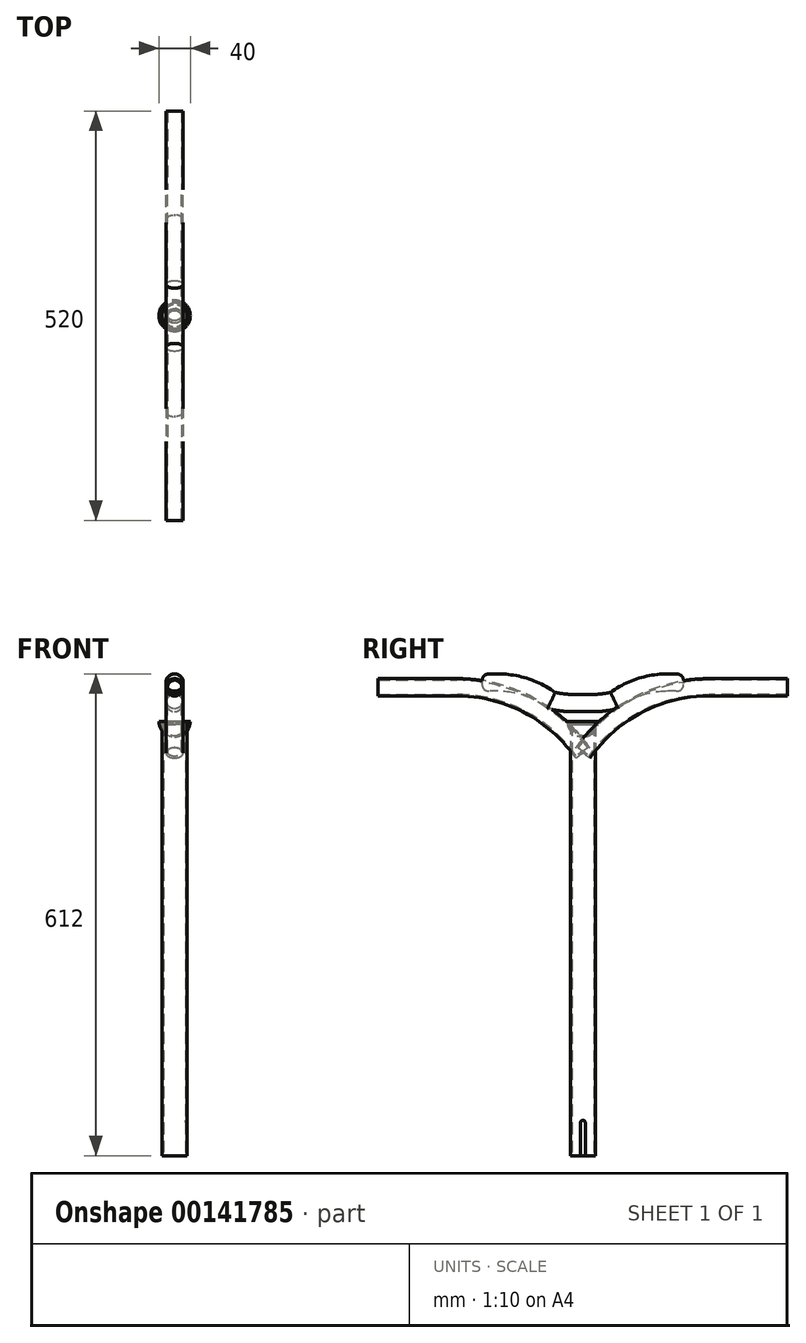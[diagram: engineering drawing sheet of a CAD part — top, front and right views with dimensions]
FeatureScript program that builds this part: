
annotation { "Feature Type Name" : "Feature", "Feature Type Description" : "" }
export const myFeature = defineFeature(function(context is Context, id is Id, definition is map)
    precondition{}
    {
        {
            var Q0;
            Q0=qCreatedBy(makeId("Top.planeOp"),FACE);
            var sketch = newSketch(context, id + "F0", { "sketchPlane" : qUnion([Q0])});
            skCircle(sketch, "E0", {"center": v(0, 0) * mm, "radius": 16 * mm});
            skSolve(sketch);
        }
        {
            var Q0;
            Q0 = qSketchRegion(id + "F0", true);
            extrude(context, id + "F1", {"entities" : qUnion([Q0]), "depth" : 550 * mm});
        }
        {
            var Q0;
            Q0=makeQuery(id+"F1.opExtrude","CAP_FACE",FACE,{"disambiguationData":[OSD([sQuery(id+"F0.wireOp",EDGE,"E0")])],"isStart":true});
            shell(context, id + "F2", {"entities" : qUnion([Q0]), "thickness" : 2 * mm});
        }
        {
            var Q0;
            Q0=qCreatedBy(makeId("Right.planeOp"),FACE);
            var sketch = newSketch(context, id + "F3", { "sketchPlane" : qUnion([Q0])});
            skLineSegment(sketch, "E1.bottom", {"start": v(-3, 0) * mm, "end": v(3, 0) * mm});
            skLineSegment(sketch, "E1.top", {"start": v(0, 45) * mm, "end": v(0, 45) * mm});
            skLineSegment(sketch, "E1.left", {"start": v(-3, 0) * mm, "end": v(-3, 42) * mm});
            skLineSegment(sketch, "E1.right", {"start": v(3, 0) * mm, "end": v(3, 42) * mm});
            skPoint(sketch, "E2.visualSharp", {"position": v(-3, 45) * mm});
            skArc(sketch, "E2.filletArc", {"start": v(0, 45) * mm, "mid": v(-2.12, 44.12) * mm, "end": v(-3, 42) * mm});
            skPoint(sketch, "E3.visualSharp", {"position": v(3, 45) * mm});
            skArc(sketch, "E3.filletArc", {"start": v(3, 42) * mm, "mid": v(2.12, 44.12) * mm, "end": v(0, 45) * mm});
            skSolve(sketch);
        }
        {
            var Q0;
            Q0 = qSketchRegion(id + "F3", true);
            extrude(context, id + "F4", {"entities" : qUnion([Q0]), "operationType" : NewBodyOperationType.REMOVE, "endBound" : BoundingType.THROUGH_ALL, "depth" : 25 * mm});
        }
        {
            var Q0;
            Q0=qCreatedBy(makeId("Right.planeOp"),FACE);
            var sketch = newSketch(context, id + "F5", { "sketchPlane" : qUnion([Q0])});
            skArc(sketch, "E4", {"start": v(160, 595) * mm, "mid": v(69.75, 572.86) * mm, "end": v(0, 511.47) * mm});
            skLineSegment(sketch, "E5", {"start": v(160, 595) * mm, "end": v(260, 595) * mm});
            skSolve(sketch);
        }
        {
            var Q0;
            Q0=sQuery(id+"F5.wireOp",VERTEX,"E5.end");
            var Q1;
            Q1=qCreatedBy(makeId("Front.planeOp"),FACE);
            cPlane(context, id + "F6", {"entities" : qUnion([Q0, Q1]), "cplaneType" : CPlaneType.PLANE_POINT, "offset" : 25 * mm, "width" : 150 * mm, "height" : 150 * mm});
        }
        {
            var Q0;
            Q0=qCreatedBy(id+"F6.planeOp",FACE);
            var sketch = newSketch(context, id + "F7", { "sketchPlane" : qUnion([Q0])});
            skCircle(sketch, "E6", {"center": v(0, 595) * mm, "radius": 11 * mm});
            skSolve(sketch);
        }
        {
            var Q0;
            Q0 = qSketchRegion(id + "F7", true);
            var Q1;
            Q1 = qConstructionFilter(qBodyType(qCreatedBy(id + "F5" ,EDGE), BodyType.WIRE), ConstructionObject.NO);
            sweep(context, id + "F8", {"profiles" : qUnion([Q0]), "path" : qUnion([Q1])});
        }
        {
            var Q0;
            Q0=makeQuery(id+"F8.opSweep","CAP_FACE",FACE,{"disambiguationData":[OSD([sQuery(id+"F5.wireOp",VERTEX,"E5.end"),sQuery(id+"F7.wireOp",EDGE,"E6")])],"isStart":true});
            shell(context, id + "F9", {"entities" : qUnion([Q0]), "thickness" : 2 * mm});
        }
        {
            var Q0;
            Q0=makeQuery(id+"F8.opSweep","SWEPT_BODY",BODY,{"disambiguationData":[OSD([sQuery(id+"F5.wireOp",EDGE,"E5"),sQuery(id+"F7.wireOp",EDGE,"E6")])]});
            var Q1;
            Q1=qCreatedBy(makeId("Front.planeOp"),FACE);
            mirror(context, id + "F10", {"entities" : qUnion([Q0]), "mirrorPlane" : qUnion([Q1])});
        }
        {
            var Q0;
            Q0=qCreatedBy(makeId("Right.planeOp"),FACE);
            var sketch = newSketch(context, id + "F11", { "sketchPlane" : qUnion([Q0])});
            skLineSegment(sketch, "E7", {"start": v(-128, 601) * mm, "end": v(-108, 601) * mm});
            skArc(sketch, "E8", {"start": v(-39.86, 578.4) * mm, "mid": v(-72.1, 595.2) * mm, "end": v(-108, 601) * mm});
            skArc(sketch, "E9", {"start": v(-39.86, 578.4) * mm, "mid": v(-26.28, 575.85) * mm, "end": v(-12.5, 575) * mm});
            skLineSegment(sketch, "E10", {"start": v(-12.5, 575) * mm, "end": v(0, 575) * mm});
            skLineSegment(sketch, "E11.MirrorCS", {"start": v(12.5, 575) * mm, "end": v(0, 575) * mm});
            skArc(sketch, "E12.MirrorCS", {"start": v(39.86, 578.4) * mm, "mid": v(26.28, 575.85) * mm, "end": v(12.5, 575) * mm});
            skArc(sketch, "E13.MirrorCS", {"start": v(39.86, 578.4) * mm, "mid": v(72.1, 595.2) * mm, "end": v(108, 601) * mm});
            skLineSegment(sketch, "E14.MirrorCS", {"start": v(128, 601) * mm, "end": v(108, 601) * mm});
            skSolve(sketch);
        }
        {
            var Q0;
            Q0=qCreatedBy(id+"F6.planeOp",FACE);
            var Q1;
            Q1=sQuery(id+"F11.wireOp",VERTEX,"E14.MirrorCS.start");
            cPlane(context, id + "F12", {"entities" : qUnion([Q0, Q1]), "cplaneType" : CPlaneType.PLANE_POINT, "offset" : 25 * mm, "width" : 150 * mm, "height" : 150 * mm});
        }
        {
            var Q0;
            Q0=qCreatedBy(id+"F12.planeOp",FACE);
            var sketch = newSketch(context, id + "F13", { "sketchPlane" : qUnion([Q0])});
            skCircle(sketch, "E15", {"center": v(0, 601) * mm, "radius": 11 * mm});
            skSolve(sketch);
        }
        {
            var Q0;
            Q0 = qSketchRegion(id + "F13", true);
            var Q1;
            Q1 = qConstructionFilter(qBodyType(qCreatedBy(id + "F11" ,EDGE), BodyType.WIRE), ConstructionObject.NO);
            sweep(context, id + "F14", {"profiles" : qUnion([Q0]), "path" : qUnion([Q1])});
        }
        {
            var Q0;
            {var subQ0=sQuery(id+"F13.wireOp",EDGE,"E15");var subQ1=sQuery(id+"F11.wireOp",VERTEX,"E7.start");Q0=makeQuery(id+"F14.boolean.opBoolean","SPLIT",EDGE,{"disambiguationData":[TD([makeQuery(id+"F10.opPattern","COPY",FACE,{"derivedFrom":makeQuery(id+"F8.opSweep","SWEPT_FACE",FACE,{"disambiguationData":[OSD([sQuery(id+"F5.wireOp",EDGE,"E4"),sQuery(id+"F7.wireOp",EDGE,"E6")])]}),"instanceName":"1"})])],"derivedFrom":makeQuery(id+"F14.opSweep","CAP_EDGE",EDGE,{"disambiguationData":[OSD([subQ1,subQ0])],"isStart":false})});}
            var Q1;
            {var subQ0=sQuery(id+"F13.wireOp",EDGE,"E15");var subQ1=sQuery(id+"F11.wireOp",VERTEX,"E14.MirrorCS.start");Q1=makeQuery(id+"F14.boolean.opBoolean","SPLIT",EDGE,{"disambiguationData":[TD([makeQuery(id+"F8.opSweep","SWEPT_FACE",FACE,{"disambiguationData":[OSD([sQuery(id+"F5.wireOp",EDGE,"E4"),sQuery(id+"F7.wireOp",EDGE,"E6")])]})])],"derivedFrom":makeQuery(id+"F14.opSweep","CAP_EDGE",EDGE,{"disambiguationData":[OSD([subQ1,subQ0])],"isStart":true})});}
            fillet(context, id + "F15", {"entities" : qUnion([Q0, Q1]), "radius" : 10 * mm, "tangentPropagation" : true, "rho" : 0.5, "crossSection" : FilletCrossSection.CONIC, "allowEdgeOverflow" : false});
        }
        {
            var Q0;
            Q0=qCreatedBy(makeId("Right.planeOp"),FACE);
            var sketch = newSketch(context, id + "F16", { "sketchPlane" : qUnion([Q0])});
            skArc(sketch, "E16", {"start": v(-20, 551.7) * mm, "mid": v(-14.04, 537.75) * mm, "end": v(0, 532) * mm});
            skLineSegment(sketch, "E17", {"start": v(0, 552) * mm, "end": v(0, 532) * mm});
            skLineSegment(sketch, "E18", {"start": v(0, 532) * mm, "end": v(0, 552) * mm});
            skLineSegment(sketch, "E19", {"start": v(-20, 551.7) * mm, "end": v(0, 552) * mm});
            skSolve(sketch);
        }
        {
            var Q0;
            Q0 = qSketchRegion(id + "F16", true);
            var Q1;
            Q1=sQuery(id+"F16.wireOp",EDGE,"E18");
            revolve(context, id + "F17", {"entities" : qUnion([Q0]), "axis" : qUnion([Q1]), "revolveType" : RevolveType.FULL});
        }
        {
            var Q0;
            Q0=makeQuery(id+"F17.opRevolve","SWEPT_FACE",FACE,{"disambiguationData":[OSD([sQuery(id+"F16.wireOp",EDGE,"E19")])]});
            shell(context, id + "F18", {"entities" : qUnion([Q0]), "thickness" : 2 * mm});
        }
    });
